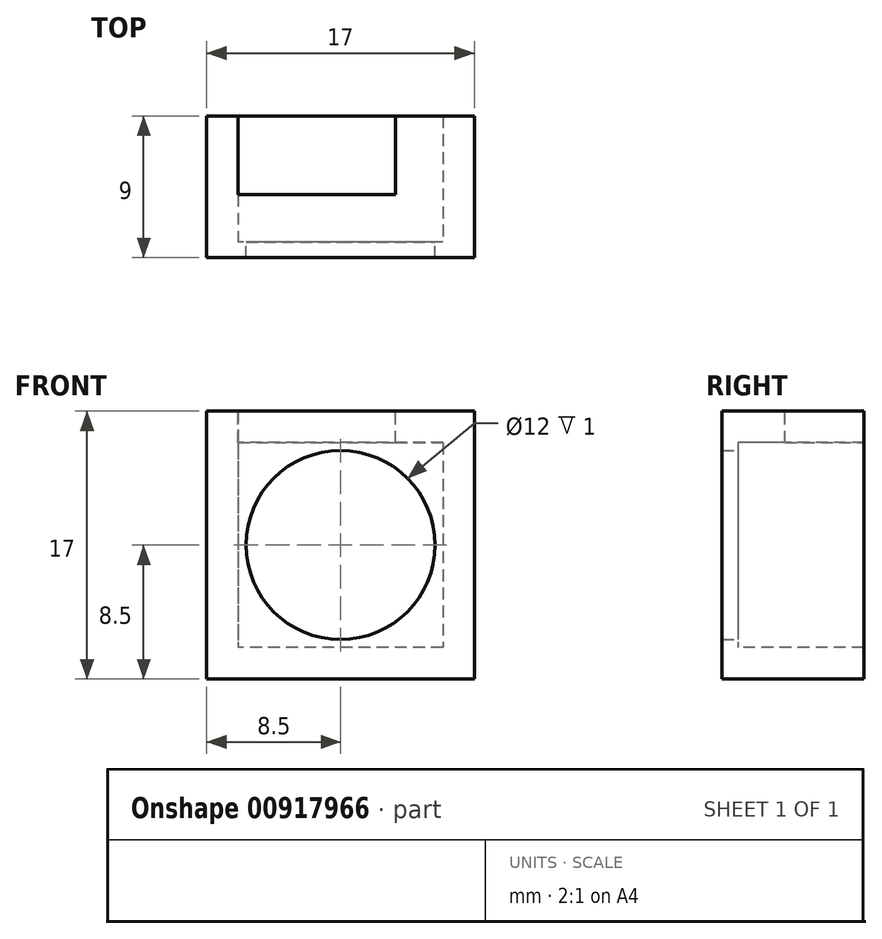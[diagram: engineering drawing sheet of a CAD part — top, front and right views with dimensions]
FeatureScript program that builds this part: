
annotation { "Feature Type Name" : "Feature", "Feature Type Description" : "" }
export const myFeature = defineFeature(function(context is Context, id is Id, definition is map)
    precondition{}
    {
        {
            var Q0;
            Q0=qCreatedBy(makeId("Front.planeOp"),FACE);
            var sketch = newSketch(context, id + "F0", { "sketchPlane" : qUnion([Q0])});
            skLineSegment(sketch, "E0.bottom", {"start": v(6.5, 6.5) * mm, "end": v(-6.5, 6.5) * mm});
            skLineSegment(sketch, "E0.top", {"start": v(6.5, -6.5) * mm, "end": v(-6.5, -6.5) * mm});
            skLineSegment(sketch, "E0.left", {"start": v(6.5, 6.5) * mm, "end": v(6.5, -6.5) * mm});
            skLineSegment(sketch, "E0.right", {"start": v(-6.5, 6.5) * mm, "end": v(-6.5, -6.5) * mm});
            skPoint(sketch, "E0.middle", {"position": v(0, 0) * mm});
            skSolve(sketch);
        }
        {
            var Q0;
            Q0 = qSketchRegion(id + "F0", true);
            extrude(context, id + "F1", {"entities" : qUnion([Q0]), "depth" : 5 * mm, "offsetDistance" : 25 * mm});
        }
        {
            var Q0;
            Q0=makeQuery(id+"F1.opExtrude","CAP_FACE",FACE,{"disambiguationData":[OSD([sQuery(id+"F0.wireOp",EDGE,"E0.bottom"),sQuery(id+"F0.wireOp",EDGE,"E0.top"),sQuery(id+"F0.wireOp",EDGE,"E0.left"),sQuery(id+"F0.wireOp",EDGE,"E0.right")])],"isStart":true});
            var sketch = newSketch(context, id + "F2", { "sketchPlane" : qUnion([Q0])});
            skCircle(sketch, "E1", {"center": v(0, 0) * mm, "radius": 6 * mm});
            skSolve(sketch);
        }
        {
            var Q0;
            Q0 = qSketchRegion(id + "F2", true);
            extrude(context, id + "F3", {"entities" : qUnion([Q0]), "operationType" : NewBodyOperationType.REMOVE, "oppositeDirection" : true, "depth" : 25 * mm, "offsetDistance" : 25 * mm});
        }
        {
            var Q0;
            Q0=makeQuery(id+"F1.opExtrude","SWEPT_FACE",FACE,{"disambiguationData":[OSD([sQuery(id+"F0.wireOp",EDGE,"E0.bottom")])]});
            var sketch = newSketch(context, id + "F4", { "sketchPlane" : qUnion([Q0])});
            skLineSegment(sketch, "E2.bottom", {"start": v(-6.5, -5) * mm, "end": v(6.5, -5) * mm});
            skLineSegment(sketch, "E2.top", {"start": v(-6.5, -4) * mm, "end": v(6.5, -4) * mm});
            skLineSegment(sketch, "E2.left", {"start": v(-6.5, -5) * mm, "end": v(-6.5, -4) * mm});
            skLineSegment(sketch, "E2.right", {"start": v(6.5, -5) * mm, "end": v(6.5, -4) * mm});
            skSolve(sketch);
        }
        {
            var Q0;
            Q0 = qSketchRegion(id + "F4", true);
            extrude(context, id + "F5", {"entities" : qUnion([Q0]), "operationType" : NewBodyOperationType.ADD, "depth" : 2 * mm, "offsetDistance" : 25 * mm});
        }
        {
            var Q0;
            Q0=makeQuery(id+"F5.boolean.opBoolean","MERGE",FACE,{"derivedFrom":[makeQuery(id+"F1.opExtrude","SWEPT_FACE",FACE,{"disambiguationData":[OSD([sQuery(id+"F0.wireOp",EDGE,"E0.left")])]}),makeQuery(id+"F5.opExtrude","SWEPT_FACE",FACE,{"disambiguationData":[OSD([sQuery(id+"F4.wireOp",EDGE,"E2.right")])]})]});
            var sketch = newSketch(context, id + "F6", { "sketchPlane" : qUnion([Q0])});
            skLineSegment(sketch, "E3.bottom", {"start": v(-5, 8.5) * mm, "end": v(-4, 8.5) * mm});
            skLineSegment(sketch, "E3.top", {"start": v(-5, -8.5) * mm, "end": v(-4, -8.5) * mm});
            skLineSegment(sketch, "E3.left", {"start": v(-5, 8.5) * mm, "end": v(-5, -8.5) * mm});
            skLineSegment(sketch, "E3.right", {"start": v(-4, 8.5) * mm, "end": v(-4, -8.5) * mm});
            skSolve(sketch);
        }
        {
            var Q0;
            Q0 = qSketchRegion(id + "F6", true);
            extrude(context, id + "F7", {"entities" : qUnion([Q0]), "operationType" : NewBodyOperationType.ADD, "depth" : 2 * mm, "offsetDistance" : 25 * mm});
        }
        {
            var Q0;
            Q0=makeQuery(id+"F5.boolean.opBoolean","MERGE",FACE,{"derivedFrom":[makeQuery(id+"F1.opExtrude","SWEPT_FACE",FACE,{"disambiguationData":[OSD([sQuery(id+"F0.wireOp",EDGE,"E0.right")])]}),makeQuery(id+"F5.opExtrude","SWEPT_FACE",FACE,{"disambiguationData":[OSD([sQuery(id+"F4.wireOp",EDGE,"E2.left")])]})]});
            var sketch = newSketch(context, id + "F8", { "sketchPlane" : qUnion([Q0])});
            skLineSegment(sketch, "E4.bottom", {"start": v(4, 8.5) * mm, "end": v(5, 8.5) * mm});
            skLineSegment(sketch, "E4.top", {"start": v(4, -6.5) * mm, "end": v(5, -6.5) * mm});
            skLineSegment(sketch, "E4.left", {"start": v(4, 8.5) * mm, "end": v(4, -6.5) * mm});
            skLineSegment(sketch, "E4.right", {"start": v(5, 8.5) * mm, "end": v(5, -6.5) * mm});
            skSolve(sketch);
        }
        {
            var Q0;
            Q0 = qSketchRegion(id + "F8", true);
            extrude(context, id + "F9", {"entities" : qUnion([Q0]), "operationType" : NewBodyOperationType.ADD, "depth" : 2 * mm, "offsetDistance" : 25 * mm});
        }
        {
            var Q0;
            Q0=makeQuery(id+"F7.opExtrude","CAP_FACE",FACE,{"disambiguationData":[OSD([sQuery(id+"F6.wireOp",EDGE,"E3.bottom"),sQuery(id+"F6.wireOp",EDGE,"E3.top"),sQuery(id+"F6.wireOp",EDGE,"E3.left"),sQuery(id+"F6.wireOp",EDGE,"E3.right")])],"isStart":true});
            extrude(context, id + "F10", {"entities" : qUnion([Q0]), "operationType" : NewBodyOperationType.ADD, "depth" : 15 * mm, "offsetDistance" : 25 * mm});
        }
        {
            var Q0;
            {var subQ0=sQuery(id+"F6.wireOp",EDGE,"E3.right");Q0=makeQuery(id+"F10.boolean.opBoolean","MERGE",FACE,{"derivedFrom":[makeQuery(id+"F9.boolean.opBoolean","MERGE",FACE,{"derivedFrom":[makeQuery(id+"F7.boolean.opBoolean","MERGE",FACE,{"derivedFrom":[makeQuery(id+"F5.opExtrude","SWEPT_FACE",FACE,{"disambiguationData":[OSD([sQuery(id+"F4.wireOp",EDGE,"E2.top")])]}),makeQuery(id+"F7.opExtrude","SWEPT_FACE",FACE,{"disambiguationData":[OSD([subQ0])]})]}),makeQuery(id+"F9.opExtrude","SWEPT_FACE",FACE,{"disambiguationData":[OSD([sQuery(id+"F8.wireOp",EDGE,"E4.left")])]})]}),makeQuery(id+"F10.opExtrude","SWEPT_FACE",FACE,{"disambiguationData":[OSD([subQ0])]})]});}
            extrude(context, id + "F11", {"entities" : qUnion([Q0]), "operationType" : NewBodyOperationType.ADD, "depth" : 8 * mm, "offsetDistance" : 25 * mm});
        }
        {
            var Q0;
            Q0=makeQuery(id+"F1.opExtrude","CAP_FACE",FACE,{"disambiguationData":[OSD([sQuery(id+"F0.wireOp",EDGE,"E0.bottom"),sQuery(id+"F0.wireOp",EDGE,"E0.top"),sQuery(id+"F0.wireOp",EDGE,"E0.left"),sQuery(id+"F0.wireOp",EDGE,"E0.right")])],"isStart":true});
            extrude(context, id + "F12", {"entities" : qUnion([Q0]), "operationType" : NewBodyOperationType.REMOVE, "oppositeDirection" : true, "depth" : 4 * mm, "offsetDistance" : 25 * mm});
        }
        {
            var Q0;
            Q0=makeQuery(id+"F11.opExtrude","CAP_FACE",FACE,{"disambiguationData":[OSD([sQuery(id+"F4.wireOp",EDGE,"E2.top"),sQuery(id+"F6.wireOp",EDGE,"E3.right"),sQuery(id+"F8.wireOp",EDGE,"E4.left")])],"isStart":false});
            var sketch = newSketch(context, id + "F13", { "sketchPlane" : qUnion([Q0])});
            skLineSegment(sketch, "E5.bottom", {"start": v(6.5, 6.5) * mm, "end": v(-3.5, 6.5) * mm});
            skLineSegment(sketch, "E5.top", {"start": v(6.5, 8.5) * mm, "end": v(-3.5, 8.5) * mm});
            skLineSegment(sketch, "E5.left", {"start": v(6.5, 6.5) * mm, "end": v(6.5, 8.5) * mm});
            skLineSegment(sketch, "E5.right", {"start": v(-3.5, 6.5) * mm, "end": v(-3.5, 8.5) * mm});
            skSolve(sketch);
        }
        {
            var Q0;
            Q0=makeQuery(id+"F13.imprint","IMPRINT",FACE,{"disambiguationData":[TD([[makeQuery(id+"F13.imprint","IMPRINT",EDGE,{"derivedFrom":sQuery(id+"F13.wireOp",EDGE,"E5.bottom")}),-1.0]])]});
            extrude(context, id + "F14", {"entities" : qUnion([Q0]), "operationType" : NewBodyOperationType.REMOVE, "oppositeDirection" : true, "depth" : 5 * mm, "offsetDistance" : 25 * mm});
        }
    });
